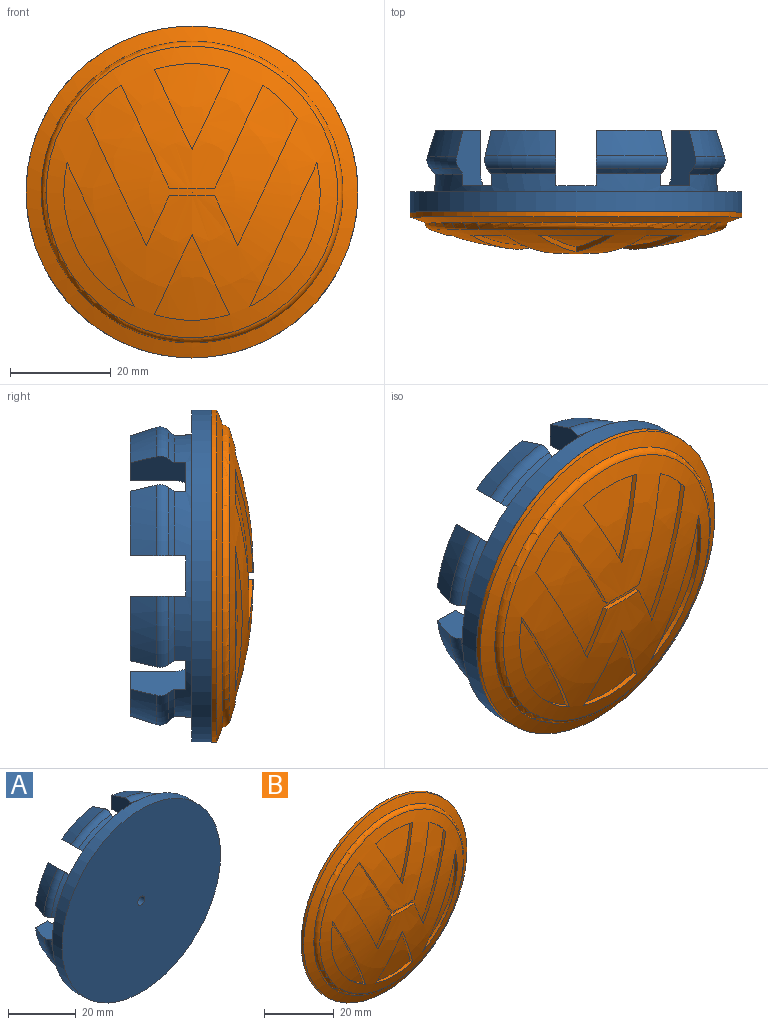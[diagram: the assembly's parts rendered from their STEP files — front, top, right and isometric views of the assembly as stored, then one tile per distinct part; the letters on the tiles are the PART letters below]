
ASSEMBLY  parts=2 mates=1
PART A: 72 faces, bbox 66.1x16.3x66.1 mm
  f0: cone r=29.17mm half-angle=45deg, axis (0,1,0), area 21.3mm2, adj f28,f36,f48,f70
  f1: cone r=29.17mm half-angle=45deg, axis (0,1,0), area 21.3mm2, adj f29,f36,f67,f69
  f2: cone r=29.17mm half-angle=45deg, axis (0,1,0), area 21.3mm2, adj f30,f36,f64,f66
  f3: cone r=29.17mm half-angle=45deg, axis (0,1,0), area 21.3mm2, adj f31,f36,f61,f63
  f4: cone r=29.17mm half-angle=45deg, axis (0,1,0), area 21.3mm2, adj f32,f36,f58,f60
  f5: cone r=29.17mm half-angle=45deg, axis (0,1,0), area 21.3mm2, adj f33,f36,f55,f57
  f6: cone r=29.17mm half-angle=45deg, axis (0,1,0), area 21.3mm2, adj f34,f36,f52,f54
  f7: cylinder r=23.12mm len=9.28mm, axis (0,1,0), area 91.1mm2, adj f14,f46,f48,f70
  f8: cylinder r=23.12mm len=9.28mm, axis (0,1,0), area 91.1mm2, adj f15,f46,f67,f69
  f9: cylinder r=23.12mm len=9.28mm, axis (0,1,0), area 91.1mm2, adj f16,f46,f64,f66
  f10: cylinder r=23.12mm len=9.28mm, axis (0,1,0), area 91.1mm2, adj f17,f46,f61,f63
  f11: cylinder r=23.12mm len=9.28mm, axis (0,1,0), area 91.1mm2, adj f18,f46,f58,f60
  f12: cylinder r=23.12mm len=9.28mm, axis (0,1,0), area 91.1mm2, adj f19,f46,f55,f57
  f13: cylinder r=23.12mm len=9.28mm, axis (0,1,0), area 91.1mm2, adj f20,f46,f52,f54
  f14: plane 12.86x8.91mm, normal (0,1,0), area 60.5mm2, adj f7,f21,f48,f70
  f15: plane 12.86x8.91mm, normal (0,1,0), area 60.5mm2, adj f8,f22,f67,f69
  f16: plane 12.86x8.91mm, normal (0,1,0), area 60.5mm2, adj f9,f23,f64,f66
  f17: plane 12.86x8.91mm, normal (0,1,0), area 60.5mm2, adj f10,f24,f61,f63
  f18: plane 12.86x8.91mm, normal (0,1,0), area 60.5mm2, adj f11,f25,f58,f60
  f19: plane 12.86x8.91mm, normal (0,1,0), area 60.5mm2, adj f12,f26,f55,f57
  f20: plane 12.86x8.91mm, normal (0,1,0), area 60.5mm2, adj f13,f27,f52,f54
  f21: cone r=28.12mm half-angle=18deg, axis (0,-1,0), area 78.7mm2, adj f14,f28,f48,f70
  f22: cone r=28.12mm half-angle=18deg, axis (0,-1,0), area 78.7mm2, adj f15,f29,f67,f69
  f23: cone r=28.12mm half-angle=18deg, axis (0,-1,0), area 78.7mm2, adj f16,f30,f64,f66
  f24: cone r=28.12mm half-angle=18deg, axis (0,-1,0), area 78.7mm2, adj f17,f31,f61,f63
  f25: cone r=28.12mm half-angle=18deg, axis (0,-1,0), area 78.7mm2, adj f18,f32,f58,f60
  f26: cone r=28.12mm half-angle=18deg, axis (0,-1,0), area 78.7mm2, adj f19,f33,f55,f57
  f27: cone r=28.12mm half-angle=18deg, axis (0,-1,0), area 78.7mm2, adj f20,f34,f52,f54
  f28: torus R=27.4mm, axis (0,1,0), area 42.1mm2, adj f0,f21,f48,f70
  f29: torus R=27.4mm, axis (0,1,0), area 42.1mm2, adj f1,f22,f67,f69
  f30: torus R=27.4mm, axis (0,1,0), area 42.1mm2, adj f2,f23,f64,f66
  f31: torus R=27.4mm, axis (0,1,0), area 42.1mm2, adj f3,f24,f61,f63
  f32: torus R=27.4mm, axis (0,1,0), area 42.1mm2, adj f4,f25,f58,f60
  f33: torus R=27.4mm, axis (0,1,0), area 42.1mm2, adj f5,f26,f55,f57
  f34: torus R=27.4mm, axis (0,1,0), area 42.1mm2, adj f6,f27,f52,f54
  f35: cone r=29.17mm half-angle=45deg, axis (0,1,0), area 21.3mm2, adj f36,f44,f49,f51
  f36: cylinder r=28.12mm len=56.25mm, axis (0,1,0), area 474.2mm2, adj f0,f1,f2,f3,f4,f5,f6,f35
  f37: plane 66x66mm, normal (0,1,0), area 936.1mm2, adj f36,f38
  f38: cylinder r=33mm len=66mm, axis (0,1,0), area 829.4mm2, adj f37,f39
  f39: plane 66x66mm, normal (0,-1,0), area 3414.1mm2, adj f38,f45
  f40: plane 40.25x40.25mm, normal (0,1,0), area 1233.9mm2, adj f46,f71
  f41: cylinder r=23.12mm len=9.28mm, axis (0,1,0), area 91.1mm2, adj f42,f46,f49,f51
  f42: plane 12.86x8.91mm, normal (0,1,0), area 60.5mm2, adj f41,f43,f49,f51
  f43: cone r=28.12mm half-angle=18deg, axis (0,-1,0), area 78.7mm2, adj f42,f44,f49,f51
  f44: torus R=27.4mm, axis (0,1,0), area 42.1mm2, adj f35,f43,f49,f51
  f45: cylinder r=1.5mm len=3mm, axis (0,-1,0), area 20.7mm2, adj f39,f71
  f46: torus R=20.12mm, axis (0,1,0), area 510.8mm2, adj f7,f8,f9,f10,f11,f12,f13,f40
  f47: plane 8x6.12mm, normal (0,1,0), area 46.3mm2, adj f36,f46,f48,f49
  f48: plane 11.07x7.7mm, normal (-1,0,0), area 65.1mm2, adj f0,f7,f14,f21,f28,f36,f46,f47
  f49: plane 11.07x7.7mm, normal (1,0,0), area 65.1mm2, adj f35,f36,f41,f42,f43,f44,f46,f47
  f50: plane 9.79x9.79mm, normal (0,1,0), area 46.3mm2, adj f36,f46,f51,f52
  f51: plane 11.07x5.47mm, normal (-0.71,0,-0.71), area 65.1mm2, adj f35,f36,f41,f42,f43,f44,f46,f50
  f52: plane 11.07x5.47mm, normal (0.71,0,0.71), area 65.1mm2, adj f6,f13,f20,f27,f34,f36,f46,f50
  f53: plane 8x6.12mm, normal (0,1,0), area 46.3mm2, adj f36,f46,f54,f55
  f54: plane 11.07x7.7mm, normal (0,0,-1), area 65.1mm2, adj f6,f13,f20,f27,f34,f36,f46,f53
  f55: plane 11.07x7.7mm, normal (0,0,1), area 65.1mm2, adj f5,f12,f19,f26,f33,f36,f46,f53
  f56: plane 9.79x9.79mm, normal (0,1,0), area 46.3mm2, adj f36,f46,f57,f58
  f57: plane 11.07x5.47mm, normal (0.71,0,-0.71), area 65.1mm2, adj f5,f12,f19,f26,f33,f36,f46,f56
  f58: plane 11.07x5.47mm, normal (-0.71,0,0.71), area 65.1mm2, adj f4,f11,f18,f25,f32,f36,f46,f56
  f59: plane 8x6.12mm, normal (0,1,0), area 46.3mm2, adj f36,f46,f60,f61
  f60: plane 11.07x7.7mm, normal (1,0,0), area 65.1mm2, adj f4,f11,f18,f25,f32,f36,f46,f59
  f61: plane 11.07x7.7mm, normal (-1,0,0), area 65.1mm2, adj f3,f10,f17,f24,f31,f36,f46,f59
  f62: plane 9.79x9.79mm, normal (0,1,0), area 46.3mm2, adj f36,f46,f63,f64
  f63: plane 11.07x5.47mm, normal (0.71,0,0.71), area 65.1mm2, adj f3,f10,f17,f24,f31,f36,f46,f62
  f64: plane 11.07x5.47mm, normal (-0.71,0,-0.71), area 65.1mm2, adj f2,f9,f16,f23,f30,f36,f46,f62
  f65: plane 8x6.12mm, normal (0,1,0), area 46.3mm2, adj f36,f46,f66,f67
  f66: plane 11.07x7.7mm, normal (0,0,1), area 65.1mm2, adj f2,f9,f16,f23,f30,f36,f46,f65
  f67: plane 11.07x7.7mm, normal (0,0,-1), area 65.1mm2, adj f1,f8,f15,f22,f29,f36,f46,f65
  f68: plane 9.79x9.79mm, normal (0,1,0), area 46.3mm2, adj f36,f46,f69,f70
  f69: plane 11.07x5.47mm, normal (-0.71,0,0.71), area 65.1mm2, adj f1,f8,f15,f22,f29,f36,f46,f68
  f70: plane 11.07x5.47mm, normal (0.71,0,-0.71), area 65.1mm2, adj f0,f7,f14,f21,f28,f36,f46,f68
  f71: cone r=1.5mm half-angle=45deg, axis (0,1,0), area 44.4mm2, adj f40,f45
PART B: 32 faces, bbox 66x8.3x66 mm
  f0: sphere r=90mm, area 634mm2, adj f2,f29
  f1: plane 66x66mm, normal (0,1,0), area 3414.1mm2, adj f2,f30
  f2: cylinder r=33mm len=66mm, axis (0,-1,0), area 207.3mm2, adj f0,f1
  f3: sphere r=91mm, area 1710.4mm2, adj f5,f6,f7,f9,f10,f12,f13,f14
  f4: sphere r=90mm, area 134.1mm2, adj f5,f6,f7
  f5: plane 16.01x7.47mm, normal (-0.91,0,-0.42), area 18mm2, adj f3,f4,f6,f7
  f6: plane 16.01x7.47mm, normal (0.91,0,-0.42), area 18mm2, adj f3,f4,f5,f7
  f7: cylinder r=25.5mm len=14.93mm, axis (0,-1,0), area 15.8mm2, adj f3,f4,f5,f6
  f8: sphere r=90mm, area 121mm2, adj f9,f10
  f9: plane 28.53x13.31mm, normal (0.91,0,-0.42), area 32.5mm2, adj f3,f8,f10
  f10: cylinder r=25.5mm len=28.53mm, axis (0,-1,0), area 35.4mm2, adj f3,f8,f9
  f11: sphere r=90mm, area 134.1mm2, adj f12,f13,f14
  f12: cylinder r=25.5mm len=14.93mm, axis (0,-1,0), area 15.8mm2, adj f3,f11,f13,f14
  f13: plane 16.01x7.47mm, normal (-0.91,0,0.42), area 18mm2, adj f3,f11,f12,f14
  f14: plane 16.01x7.47mm, normal (0.91,0,0.42), area 18mm2, adj f3,f11,f12,f13
  f15: sphere r=90mm, area 488.4mm2, adj f16,f17,f18,f19,f20,f21,f22,f23
  f16: plane 25.26x11.78mm, normal (0.91,0,0.42), area 28.4mm2, adj f3,f15,f17,f18
  f17: plane 9.9x4.62mm, normal (-0.91,0,0.42), area 11mm2, adj f3,f15,f16,f19
  f18: cylinder r=25.5mm len=6.83mm, axis (0,-1,0), area 10mm2, adj f3,f15,f16,f25
  f19: plane 9x1.11mm, normal (0,0,1), area 9mm2, adj f3,f15,f17,f20
  f20: plane 9.9x4.62mm, normal (0.91,0,0.42), area 11mm2, adj f3,f15,f19,f21
  f21: plane 25.26x11.78mm, normal (-0.91,0,0.42), area 28.4mm2, adj f3,f15,f20,f22
  f22: cylinder r=25.5mm len=6.83mm, axis (0,-1,0), area 10mm2, adj f3,f15,f21,f23
  f23: plane 20.52x9.57mm, normal (0.91,0,-0.42), area 23mm2, adj f3,f15,f22,f24
  f24: plane 9x1.11mm, normal (0,0,-1), area 9mm2, adj f3,f15,f23,f25
  f25: plane 20.52x9.57mm, normal (-0.91,0,-0.42), area 23mm2, adj f3,f15,f18,f24
  f26: sphere r=90mm, area 121mm2, adj f27,f28
  f27: plane 28.53x13.31mm, normal (-0.91,0,-0.42), area 32.5mm2, adj f3,f26,f28
  f28: cylinder r=25.5mm len=28.53mm, axis (0,-1,0), area 35.4mm2, adj f3,f26,f27
  f29: torus R=28.5mm, axis (0,-1,0), area 346.1mm2, adj f0,f3
  f30: cylinder r=1.5mm len=6mm, axis (0,1,0), area 56.5mm2, adj f1,f31
  f31: plane 3x3mm, normal (0,1,0), area 7.1mm2, adj f30
PLACE A t=(-20.7,60.61,3.59)mm
PLACE B t=(-20.7,43.41,3.59)mm
MATE fastened B.f2 <-> A.f0  axis (0,1,0) through (-20.7,44.41,3.59)mm
